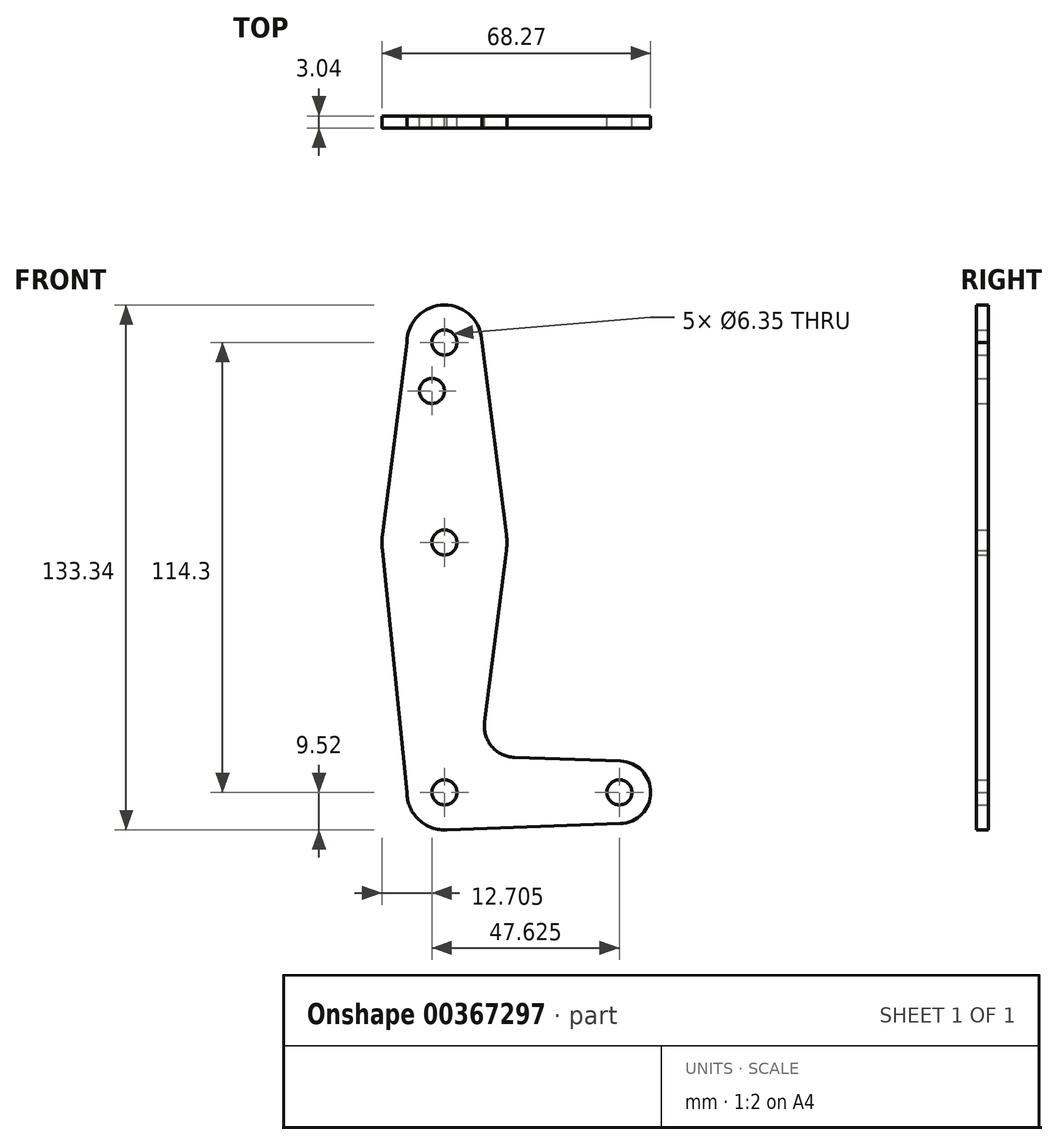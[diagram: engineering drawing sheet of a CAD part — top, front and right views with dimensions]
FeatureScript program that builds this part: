
annotation { "Feature Type Name" : "Feature", "Feature Type Description" : "" }
export const myFeature = defineFeature(function(context is Context, id is Id, definition is map)
    precondition{}
    {
        {
            var Q0;
            Q0=qCreatedBy(makeId("Front.planeOp"),FACE);
            var sketch = newSketch(context, id + "F0", { "sketchPlane" : qUnion([Q0])});
            skCircle(sketch, "E0", {"center": v(0, 50.8) * mm, "radius": 9.53 * mm});
            skCircle(sketch, "E1", {"center": v(0, 0) * mm, "radius": 15.88 * mm});
            skCircle(sketch, "E2", {"center": v(0, -63.5) * mm, "radius": 9.53 * mm});
            skCircle(sketch, "E3", {"center": v(44.45, -63.5) * mm, "radius": 7.94 * mm});
            skLineSegment(sketch, "E4", {"start": v(0, 50.8) * mm, "end": v(0, -63.5) * mm, "construction": true});
            skLineSegment(sketch, "E5", {"start": v(44.45, -63.5) * mm, "end": v(0, -63.5) * mm, "construction": true});
            skLineSegment(sketch, "E6", {"start": v(17.79, -54.6) * mm, "end": v(44.73, -55.56) * mm});
            skLineSegment(sketch, "E7", {"start": v(0, -73.03) * mm, "end": v(44.73, -71.44) * mm});
            skLineSegment(sketch, "E8", {"start": v(-9.53, 50.8) * mm, "end": v(-15.75, 2) * mm});
            skLineSegment(sketch, "E9", {"start": v(-9.53, -63.5) * mm, "end": v(-15.75, -2) * mm});
            skLineSegment(sketch, "E10", {"start": v(9.52, 50.8) * mm, "end": v(15.75, 2) * mm});
            skLineSegment(sketch, "E11", {"start": v(10.18, -45.66) * mm, "end": v(15.75, -2) * mm});
            skCircle(sketch, "E12", {"center": v(0, 50.8) * mm, "radius": 3.18 * mm});
            skCircle(sketch, "E13", {"center": v(0, -63.5) * mm, "radius": 3.18 * mm});
            skCircle(sketch, "E14", {"center": v(44.45, -63.5) * mm, "radius": 3.18 * mm});
            skCircle(sketch, "E15", {"center": v(0, 0) * mm, "radius": 3.18 * mm});
            skCircle(sketch, "E16", {"center": v(-3.17, 38.5) * mm, "radius": 3.18 * mm});
            skPoint(sketch, "E17.newPointB", {"position": v(0, -53.98) * mm});
            skArc(sketch, "E17.filletArc", {"start": v(10.18, -45.66) * mm, "mid": v(12, -51.8) * mm, "end": v(17.79, -54.6) * mm});
            skSolve(sketch);
        }
        {
            var Q0;
            Q0 = qSketchRegion(id + "F0", true);
            extrude(context, id + "F1", {"entities" : qUnion([Q0]), "endBound" : BoundingType.SYMMETRIC, "depth" : 3.05 * mm});
        }
    });
